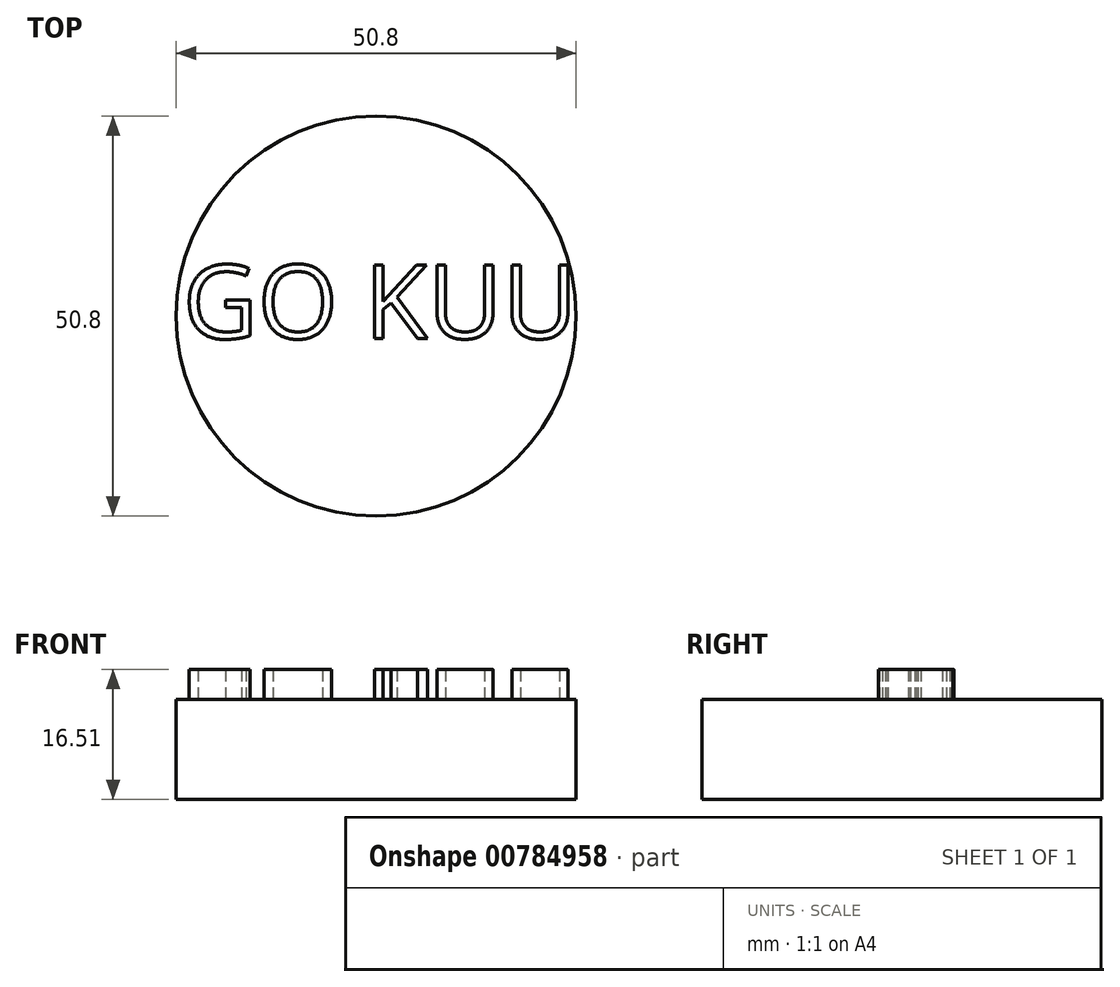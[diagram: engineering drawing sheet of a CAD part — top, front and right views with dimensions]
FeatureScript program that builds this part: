
annotation { "Feature Type Name" : "Feature", "Feature Type Description" : "" }
export const myFeature = defineFeature(function(context is Context, id is Id, definition is map)
    precondition{}
    {
        {
            var Q0;
            Q0=qCreatedBy(makeId("Top.planeOp"),FACE);
            var sketch = newSketch(context, id + "F0", { "sketchPlane" : qUnion([Q0])});
            skCircle(sketch, "E0", {"center": v(0, 0) * mm, "radius": 25.4 * mm});
            skSolve(sketch);
        }
        {
            var Q0;
            Q0 = qSketchRegion(id + "F0", true);
            extrude(context, id + "F1", {"entities" : qUnion([Q0]), "depth" : 12.7 * mm, "offsetDistance" : 25.4 * mm});
        }
        {
            var Q0;
            Q0=makeQuery(id+"F1.opExtrude","CAP_FACE",FACE,{"disambiguationData":[OSD([sQuery(id+"F0.wireOp",EDGE,"E0")])],"isStart":false});
            var sketch = newSketch(context, id + "F2", { "sketchPlane" : qUnion([Q0])});
            skText(sketch, "E1", { "text": "GO KUU", "fontName": "OpenSans-Regular.ttf"});
            const initialGuessF2  = {"E1": [-0.02454, -0.00285, 1, 0, 0.0094]};
            skSetInitialGuess(sketch, initialGuessF2);
            skSolve(sketch);
        }
        {
            var Q0;
            Q0 = qSketchRegion(id + "F2", true);
            extrude(context, id + "F3", {"entities" : qUnion([Q0]), "operationType" : NewBodyOperationType.ADD, "depth" : 3.8 * mm, "offsetDistance" : 25.4 * mm});
        }
    });
